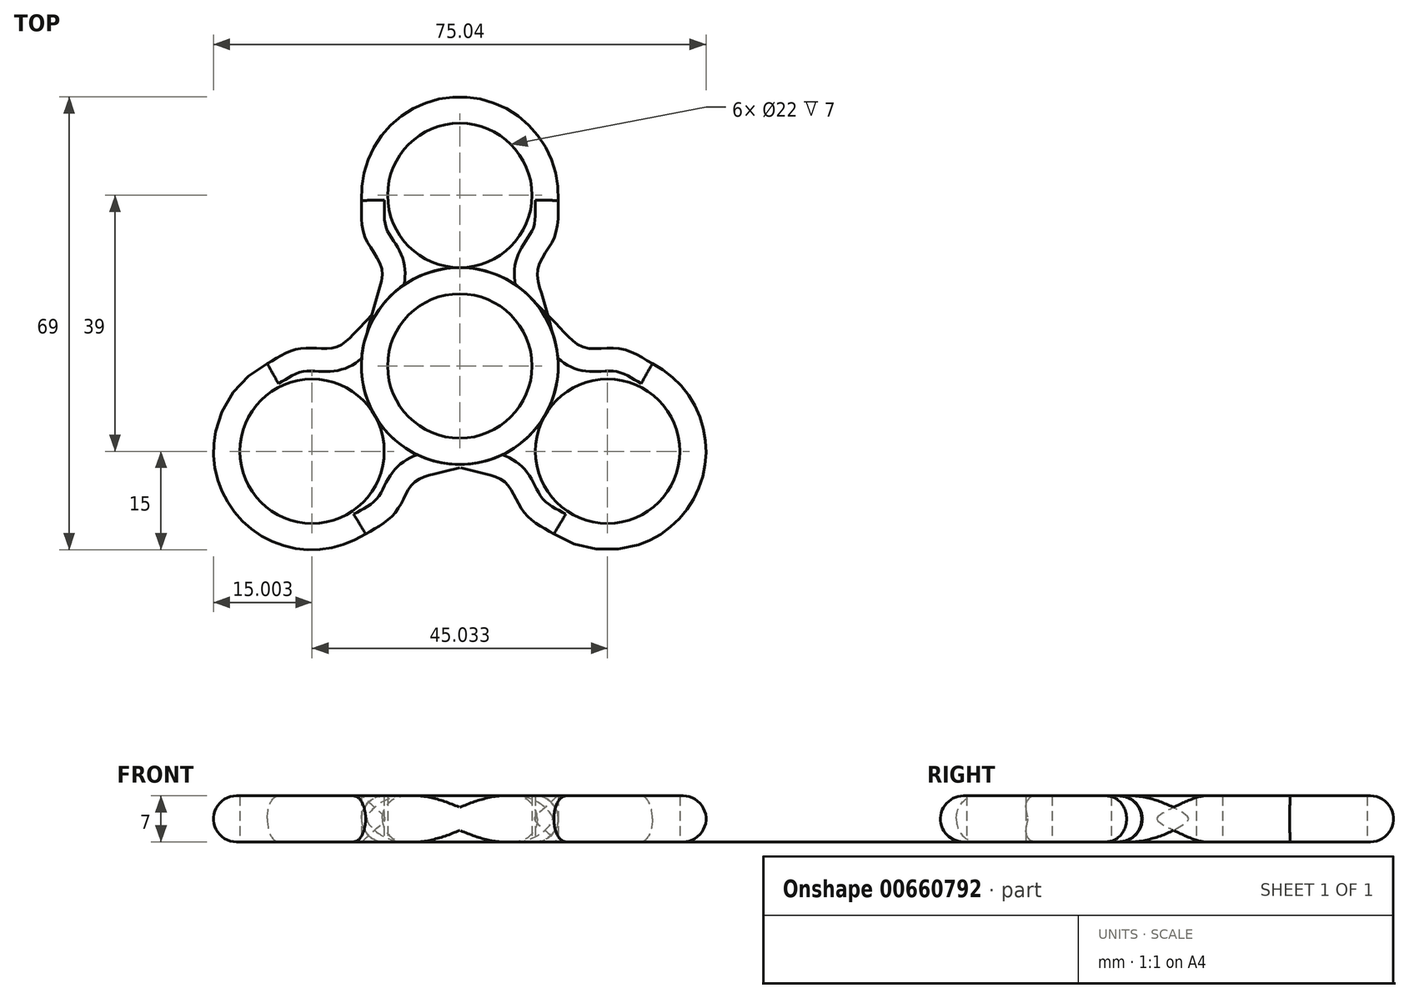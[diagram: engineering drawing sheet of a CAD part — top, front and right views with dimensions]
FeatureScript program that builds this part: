
annotation { "Feature Type Name" : "Feature", "Feature Type Description" : "" }
export const myFeature = defineFeature(function(context is Context, id is Id, definition is map)
    precondition{}
    {
        {
            var Q0;
            Q0=qCreatedBy(makeId("Top.planeOp"),FACE);
            var sketch = newSketch(context, id + "F0", { "sketchPlane" : qUnion([Q0])});
            skCircle(sketch, "E0", {"center": v(0, 0) * mm, "radius": 11 * mm});
            skLineSegment(sketch, "E1", {"start": v(0, 0) * mm, "end": v(0, 26) * mm});
            skCircle(sketch, "E2", {"center": v(0, 26) * mm, "radius": 11 * mm});
            skArc(sketch, "E3", {"start": v(14.98, 25.22) * mm, "mid": v(0, 41) * mm, "end": v(-14.98, 25.22) * mm});
            skArc(sketch, "E4", {"start": v(-14.17, 4.91) * mm, "mid": v(0, -15) * mm, "end": v(14.17, 4.91) * mm});
            skFitSpline(sketch, "E5", {"points": [v(-14.98, 25.22) * mm, v(-14.36, 19.47) * mm, v(-11.95, 15.09) * mm, v(-12.53, 10.78) * mm, v(-14.17, 4.91) * mm], "startDerivative": vector(-0.59, -23.1) * mm, "endDerivative": vector(-6.02, -22.55) * mm});
            skFitSpline(sketch, "E6.MirrorCS", {"points": [v(14.98, 25.22) * mm, v(14.36, 19.47) * mm, v(11.95, 15.09) * mm, v(12.53, 10.78) * mm, v(14.17, 4.91) * mm], "startDerivative": vector(0.59, -23.1) * mm, "endDerivative": vector(6.02, -22.55) * mm});
            skPoint(sketch, "E7.orphan", {"position": v(-10.22, 10.98) * mm});
            skPoint(sketch, "E8.orphan", {"position": v(10.22, 10.98) * mm});
            skSolve(sketch);
        }
        {
            var Q0;
            Q0=makeQuery(id+"F0.imprint","IMPRINT",FACE,{"disambiguationData":[TD([[makeQuery(id+"F0.imprint","IMPRINT",EDGE,{"derivedFrom":sQuery(id+"F0.wireOp",EDGE,"E0")}),-1.0]])]});
            extrude(context, id + "F1", {"entities" : qUnion([Q0]), "depth" : 7 * mm, "offsetDistance" : 25 * mm});
        }
        {
            var Q0;
            Q0=makeQuery(id+"F1.opExtrude","SWEPT_BODY",BODY,{"disambiguationData":[OSD([sQuery(id+"F0.wireOp",EDGE,"E0"),sQuery(id+"F0.wireOp",EDGE,"E2"),sQuery(id+"F0.wireOp",EDGE,"E3"),sQuery(id+"F0.wireOp",EDGE,"E4"),sQuery(id+"F0.wireOp",EDGE,"E5"),sQuery(id+"F0.wireOp",EDGE,"E6.MirrorCS")])]});
            var Q1;
            Q1=makeQuery(id+"F1.opExtrude","CAP_EDGE",EDGE,{"disambiguationData":[OSD([sQuery(id+"F0.wireOp",EDGE,"E0")])],"isStart":false});
            circularPattern(context, id + "F2", {"entities" : qUnion([Q0]), "axis" : qUnion([Q1]), "angle" : 360 * degree, "instanceCount" : 3, "equalSpace" : true});
        }
        {
            var Q0;
            Q0=makeQuery(id+"F1.opExtrude","CAP_EDGE",EDGE,{"disambiguationData":[OSD([sQuery(id+"F0.wireOp",EDGE,"E3")])],"isStart":false});
            var Q1;
            Q1=makeQuery(id+"F1.opExtrude","CAP_EDGE",EDGE,{"disambiguationData":[OSD([sQuery(id+"F0.wireOp",EDGE,"E5")])],"isStart":false});
            var Q2;
            Q2=makeQuery(id+"F2.opPattern","COPY",EDGE,{"derivedFrom":makeQuery(id+"F1.opExtrude","CAP_EDGE",EDGE,{"disambiguationData":[OSD([sQuery(id+"F0.wireOp",EDGE,"E6.MirrorCS")])],"isStart":false}),"instanceName":"1"});
            var Q3;
            Q3=makeQuery(id+"F2.opPattern","COPY",EDGE,{"derivedFrom":makeQuery(id+"F1.opExtrude","CAP_EDGE",EDGE,{"disambiguationData":[OSD([sQuery(id+"F0.wireOp",EDGE,"E3")])],"isStart":false}),"instanceName":"1"});
            var Q4;
            Q4=makeQuery(id+"F2.opPattern","COPY",EDGE,{"derivedFrom":makeQuery(id+"F1.opExtrude","CAP_EDGE",EDGE,{"disambiguationData":[OSD([sQuery(id+"F0.wireOp",EDGE,"E5")])],"isStart":false}),"instanceName":"1"});
            var Q5;
            Q5=makeQuery(id+"F2.opPattern","COPY",EDGE,{"derivedFrom":makeQuery(id+"F1.opExtrude","CAP_EDGE",EDGE,{"disambiguationData":[OSD([sQuery(id+"F0.wireOp",EDGE,"E6.MirrorCS")])],"isStart":false}),"instanceName":"2"});
            var Q6;
            Q6=makeQuery(id+"F2.opPattern","COPY",EDGE,{"derivedFrom":makeQuery(id+"F1.opExtrude","CAP_EDGE",EDGE,{"disambiguationData":[OSD([sQuery(id+"F0.wireOp",EDGE,"E3")])],"isStart":false}),"instanceName":"2"});
            var Q7;
            Q7=makeQuery(id+"F2.opPattern","COPY",EDGE,{"derivedFrom":makeQuery(id+"F1.opExtrude","CAP_EDGE",EDGE,{"disambiguationData":[OSD([sQuery(id+"F0.wireOp",EDGE,"E5")])],"isStart":false}),"instanceName":"2"});
            var Q8;
            Q8=makeQuery(id+"F1.opExtrude","CAP_EDGE",EDGE,{"disambiguationData":[OSD([sQuery(id+"F0.wireOp",EDGE,"E6.MirrorCS")])],"isStart":false});
            var Q9;
            Q9=makeQuery(id+"F2.opPattern","COPY",EDGE,{"derivedFrom":makeQuery(id+"F1.opExtrude","CAP_EDGE",EDGE,{"disambiguationData":[OSD([sQuery(id+"F0.wireOp",EDGE,"E3")])],"isStart":true}),"instanceName":"1"});
            var Q10;
            Q10=makeQuery(id+"F2.opPattern","COPY",EDGE,{"derivedFrom":makeQuery(id+"F1.opExtrude","CAP_EDGE",EDGE,{"disambiguationData":[OSD([sQuery(id+"F0.wireOp",EDGE,"E5")])],"isStart":true}),"instanceName":"1"});
            var Q11;
            Q11=makeQuery(id+"F2.opPattern","COPY",EDGE,{"derivedFrom":makeQuery(id+"F1.opExtrude","CAP_EDGE",EDGE,{"disambiguationData":[OSD([sQuery(id+"F0.wireOp",EDGE,"E3")])],"isStart":true}),"instanceName":"2"});
            var Q12;
            Q12=makeQuery(id+"F2.opPattern","COPY",EDGE,{"derivedFrom":makeQuery(id+"F1.opExtrude","CAP_EDGE",EDGE,{"disambiguationData":[OSD([sQuery(id+"F0.wireOp",EDGE,"E5")])],"isStart":true}),"instanceName":"2"});
            var Q13;
            Q13=makeQuery(id+"F1.opExtrude","CAP_EDGE",EDGE,{"disambiguationData":[OSD([sQuery(id+"F0.wireOp",EDGE,"E3")])],"isStart":true});
            var Q14;
            Q14=makeQuery(id+"F1.opExtrude","CAP_EDGE",EDGE,{"disambiguationData":[OSD([sQuery(id+"F0.wireOp",EDGE,"E5")])],"isStart":true});
            var Q15;
            Q15=makeQuery(id+"F2.opPattern","COPY",EDGE,{"derivedFrom":makeQuery(id+"F1.opExtrude","CAP_EDGE",EDGE,{"disambiguationData":[OSD([sQuery(id+"F0.wireOp",EDGE,"E6.MirrorCS")])],"isStart":true}),"instanceName":"1"});
            var Q16;
            Q16=makeQuery(id+"F2.opPattern","COPY",EDGE,{"derivedFrom":makeQuery(id+"F1.opExtrude","CAP_EDGE",EDGE,{"disambiguationData":[OSD([sQuery(id+"F0.wireOp",EDGE,"E6.MirrorCS")])],"isStart":true}),"instanceName":"2"});
            fillet(context, id + "F3", {"entities" : qUnion([Q0, Q1, Q2, Q3, Q4, Q5, Q6, Q7, Q8, Q9, Q10, Q11, Q12, Q13, Q14, Q15, Q16]), "radius" : 3.5 * mm, "tangentPropagation" : true, "allowEdgeOverflow" : false});
        }
    });
